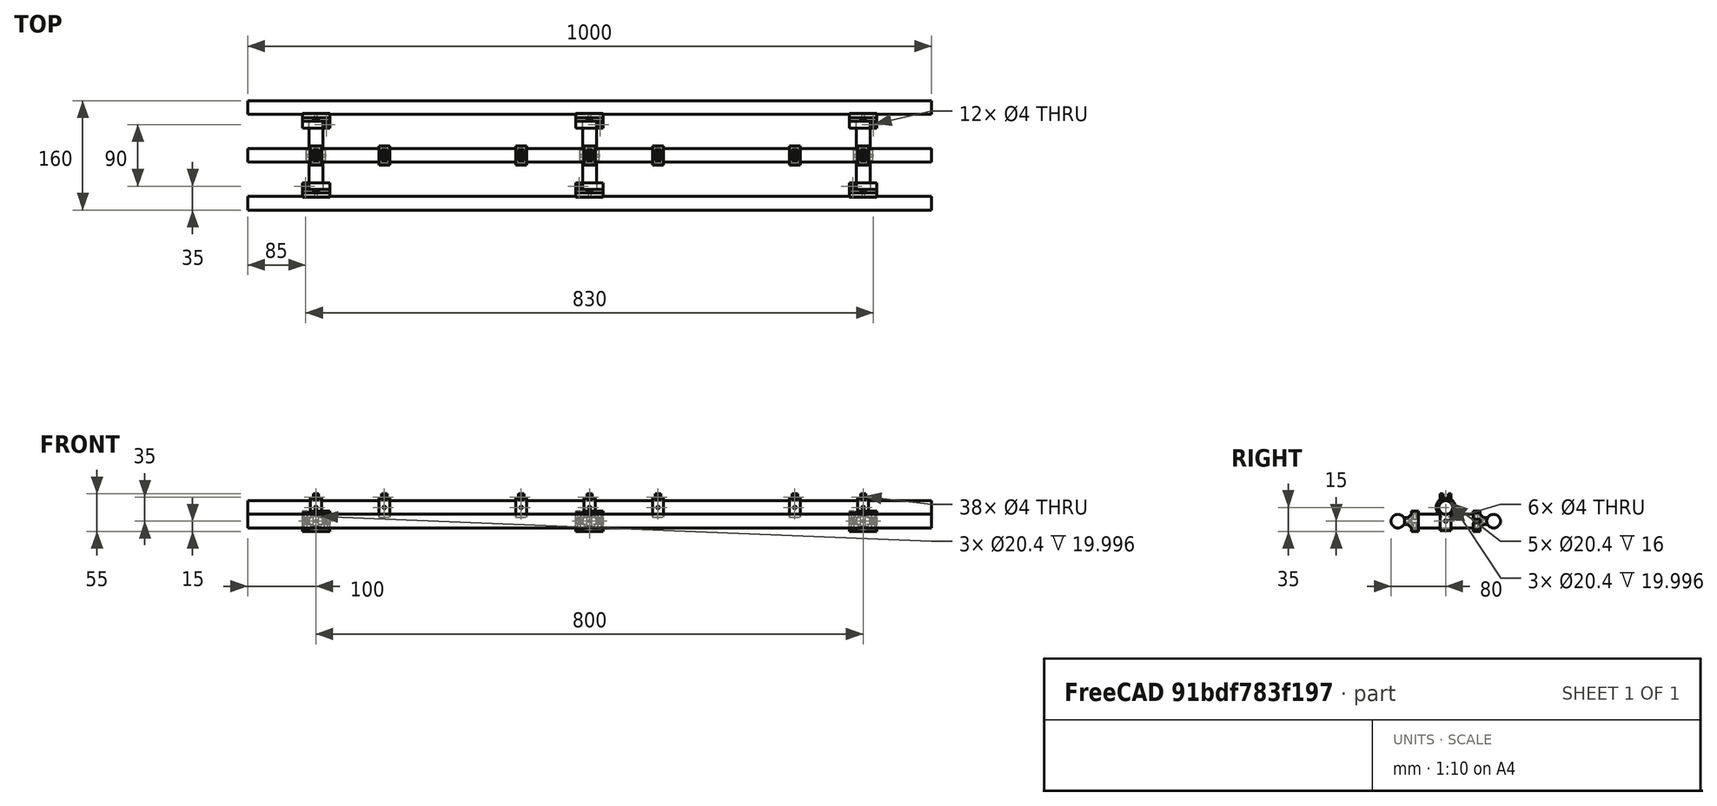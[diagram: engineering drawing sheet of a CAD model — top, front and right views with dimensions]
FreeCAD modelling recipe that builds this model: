
FCSTD DOCUMENT  (FreeCAD 0.17R13522 (Git))
Label: rail
License: All rights reserved
LicenseURL: http://en.wikipedia.org/wiki/All_rights_reserved
objects: Part::FeaturePython×14, Part::Cylinder×6, App::Part×1
note: 20 computed .brp shape members not serialized (recipe doc carries the construction recipe); baked Part::Feature solids carry a one-line shape summary decoded from their .brp

FEATURE [Part::Cylinder] Cylinder
  Angle = 360
  AttacherType = Attacher::AttachEngine3D
  Height = 1000
  Placement = pos=(-500,-70,0) rot=(0,1,0;1.5708rad)
  Radius = 10
FEATURE [Part::Cylinder] Cylinder001
  Angle = 360
  AttacherType = Attacher::AttachEngine3D
  Height = 1000
  Placement = pos=(-500,70,0) rot=(0,1,0;1.5708rad)
  Radius = 10
FEATURE [Part::Cylinder] Cylinder002
  Angle = 360
  AttacherType = Attacher::AttachEngine3D
  Height = 100
  Placement = pos=(0,-50,0) rot=(1,0,0;4.71239rad)
  Radius = 10
FEATURE [Part::Cylinder] Cylinder003
  Angle = 360
  AttacherType = Attacher::AttachEngine3D
  Height = 100
  Placement = pos=(-400,-50,0) rot=(-1,0,0;1.5708rad)
  Radius = 10
FEATURE [Part::Cylinder] Cylinder004
  Angle = 360
  AttacherType = Attacher::AttachEngine3D
  Height = 100
  Placement = pos=(400,-50,0) rot=(-1,0,0;1.5708rad)
  Radius = 10
FEATURE [Part::Cylinder] Cylinder005
  Angle = 360
  AttacherType = Attacher::AttachEngine3D
  Height = 1000
  Placement = pos=(-500,0,20) rot=(0,1,0;1.5708rad)
  Radius = 10
FEATURE [App::Part] Part  label="Pipes"
  Group = -> [Cylinder,Cylinder001,Cylinder002,Cylinder003,Cylinder004,Cylinder005]
  License = CC BY 3.0
  LicenseURL = http://creativecommons.org/licenses/by/3.0/
  Origin = -> Origin
FEATURE [Part::FeaturePython] connector_rack_sleeper_01  # a2plus imported part (geometry in sourceFile) (typed FeaturePython)
  Placement = pos=(0,0,10) rot=(0,1,0;1.5708rad)
  fixedPosition = true
  sourceFile = <userpath>/repo/mavis/cad/rail/connector-rack-sleeper.fcstd
  timeLastImport = 1.54321e+09
  updateColors = true
FEATURE [Part::FeaturePython] connector_rack_sleeper_002  # a2plus imported part (geometry in sourceFile) (typed FeaturePython)
  Placement = pos=(-400,0,10) rot=(0,1,0;1.5708rad)
  fixedPosition = true
  sourceFile = <userpath>/repo/mavis/cad/rail/connector-rack-sleeper.fcstd
  timeLastImport = 1.54321e+09
  updateColors = true
FEATURE [Part::FeaturePython] connector_rack_sleeper_003  # a2plus imported part (geometry in sourceFile) (typed FeaturePython)
  Placement = pos=(400,0,10) rot=(0,1,0;1.5708rad)
  fixedPosition = true
  sourceFile = <userpath>/repo/mavis/cad/rail/connector-rack-sleeper.fcstd
  timeLastImport = 1.54321e+09
  updateColors = true
FEATURE [Part::FeaturePython] connector_rack_01  # a2plus imported part (geometry in sourceFile) (typed FeaturePython)
  Placement = pos=(0,0,10) rot=(0,1,0;1.5708rad)
  fixedPosition = false
  sourceFile = <userpath>/repo/mavis/cad/rail/connector-rack.fcstd
  timeLastImport = 1.54321e+09
  updateColors = true
FEATURE [Part::FeaturePython] connector_rack_002  # a2plus imported part (geometry in sourceFile) (typed FeaturePython)
  Placement = pos=(-100,0,10) rot=(0,1,0;1.5708rad)
  fixedPosition = false
  sourceFile = <userpath>/repo/mavis/cad/rail/connector-rack.fcstd
  timeLastImport = 1.54321e+09
  updateColors = true
FEATURE [Part::FeaturePython] connector_rack_003  # a2plus imported part (geometry in sourceFile) (typed FeaturePython)
  Placement = pos=(-300,0,10) rot=(0,1,0;1.5708rad)
  fixedPosition = false
  sourceFile = <userpath>/repo/mavis/cad/rail/connector-rack.fcstd
  timeLastImport = 1.54321e+09
  updateColors = true
FEATURE [Part::FeaturePython] connector_rack_004  # a2plus imported part (geometry in sourceFile) (typed FeaturePython)
  Placement = pos=(100,0,10) rot=(0,1,0;1.5708rad)
  fixedPosition = false
  sourceFile = <userpath>/repo/mavis/cad/rail/connector-rack.fcstd
  timeLastImport = 1.54321e+09
  updateColors = true
FEATURE [Part::FeaturePython] connector_rack_005  # a2plus imported part (geometry in sourceFile) (typed FeaturePython)
  Placement = pos=(300,0,10) rot=(0,1,0;1.5708rad)
  fixedPosition = false
  sourceFile = <userpath>/repo/mavis/cad/rail/connector-rack.fcstd
  timeLastImport = 1.54321e+09
  updateColors = true
FEATURE [Part::FeaturePython] connector_sleeper_01  # a2plus imported part (geometry in sourceFile) (typed FeaturePython)
  Placement = pos=(400,-45,0) rot=(1,0,0;1.5708rad)
  fixedPosition = false
  sourceFile = <userpath>/repo/mavis/cad/rail/connector-sleeper.fcstd
  timeLastImport = 1.54321e+09
  updateColors = true
FEATURE [Part::FeaturePython] connector_sleeper_002  # a2plus imported part (geometry in sourceFile) (typed FeaturePython)
  Placement = pos=(400,45,0) rot=(0,0.707107,0.707107;3.14159rad)
  fixedPosition = false
  sourceFile = <userpath>/repo/mavis/cad/rail/connector-sleeper.fcstd
  timeLastImport = 1.54321e+09
  updateColors = true
FEATURE [Part::FeaturePython] connector_sleeper_003  # a2plus imported part (geometry in sourceFile) (typed FeaturePython)
  Placement = pos=(-400,-45,0) rot=(1,0,0;1.5708rad)
  fixedPosition = false
  sourceFile = <userpath>/repo/mavis/cad/rail/connector-sleeper.fcstd
  timeLastImport = 1.54321e+09
  updateColors = true
FEATURE [Part::FeaturePython] connector_sleeper_004  # a2plus imported part (geometry in sourceFile) (typed FeaturePython)
  Placement = pos=(-400,45,0) rot=(0,0.707107,0.707107;3.14159rad)
  fixedPosition = false
  sourceFile = <userpath>/repo/mavis/cad/rail/connector-sleeper.fcstd
  timeLastImport = 1.54321e+09
  updateColors = true
FEATURE [Part::FeaturePython] connector_sleeper_005  # a2plus imported part (geometry in sourceFile) (typed FeaturePython)
  Placement = pos=(0,-45,0) rot=(1,0,0;1.5708rad)
  fixedPosition = false
  sourceFile = <userpath>/repo/mavis/cad/rail/connector-sleeper.fcstd
  timeLastImport = 1.54321e+09
  updateColors = true
FEATURE [Part::FeaturePython] connector_sleeper_006  # a2plus imported part (geometry in sourceFile) (typed FeaturePython)
  Placement = pos=(0,45,0) rot=(0,0.707107,0.707107;3.14159rad)
  fixedPosition = false
  sourceFile = <userpath>/repo/mavis/cad/rail/connector-sleeper.fcstd
  timeLastImport = 1.54321e+09
  updateColors = true
